FCSTD DOCUMENT  (FreeCAD 0.16R6712 (Git))
Label: Extruder_Assembly
License: CreativeCommons Attribution-ShareAlike
LicenseURL: http://creativecommons.org/licenses/by-sa/4.0/
objects: Part::FeaturePython×61, Part::Feature×27, Part::Compound×1
note: 89 computed .brp shape members not serialized (recipe doc carries the construction recipe); baked Part::Feature solids carry a one-line shape summary decoded from their .brp

FEATURE [Part::FeaturePython] tpge_extruderbase_01  # a2plus imported part (geometry in sourceFile) (typed FeaturePython)
  fixedPosition = true
  sourceFile = <userpath>/Downloads/The_Toranado_Precision_Geared_1.75mm_Extruder/files/tpge-extruderbase.FCStd
  timeLastImport = 1457562951
  updateColors = true
FEATURE [Part::FeaturePython] Knurl_Nut_01  # a2plus imported part (geometry in sourceFile) (typed FeaturePython)
  Placement = pos=(45.8,-17.25,27.12) rot=(0,1,0;1.5708rad)
  fixedPosition = false
  sourceFile = <userpath>/Downloads/The_Toranado_Precision_Geared_1.75mm_Extruder/files/Knurl Nut.FCStd
  timeLastImport = 1457566460
  updateColors = true
FEATURE [Part::FeaturePython] Knurl_Nut_002  # a2plus imported part (geometry in sourceFile) (typed FeaturePython)
  Placement = pos=(45.8,-17.25,4.12) rot=(0,1,0;1.5708rad)
  fixedPosition = false
  sourceFile = <userpath>/Downloads/The_Toranado_Precision_Geared_1.75mm_Extruder/files/Knurl Nut.FCStd
  timeLastImport = 1457566460
  updateColors = true
FEATURE [Part::FeaturePython] Knurl_Nut_003  # a2plus imported part (geometry in sourceFile) (typed FeaturePython)
  Placement = pos=(45.8,5.75,4.12) rot=(0,1,0;1.5708rad)
  fixedPosition = false
  sourceFile = <userpath>/Downloads/The_Toranado_Precision_Geared_1.75mm_Extruder/files/Knurl Nut.FCStd
  timeLastImport = 1457566460
  updateColors = true
FEATURE [Part::FeaturePython] Knurl_Nut_004  # a2plus imported part (geometry in sourceFile) (typed FeaturePython)
  Placement = pos=(-6.1,-20,6.7) rot=(0,1,0;1.5708rad)
  fixedPosition = false
  sourceFile = <userpath>/Downloads/The_Toranado_Precision_Geared_1.75mm_Extruder/files/Knurl Nut.FCStd
  timeLastImport = 1457566460
  updateColors = true
FEATURE [Part::FeaturePython] Knurl_Nut_005  # a2plus imported part (geometry in sourceFile) (typed FeaturePython)
  Placement = pos=(-2.8,-20,26) rot=(0,1,0;1.5708rad)
  fixedPosition = false
  sourceFile = <userpath>/Downloads/The_Toranado_Precision_Geared_1.75mm_Extruder/files/Knurl Nut.FCStd
  timeLastImport = 1457566460
  updateColors = true
FEATURE [Part::FeaturePython] PTFE_tubing_01  # a2plus imported part (geometry in sourceFile) (typed FeaturePython)
  Placement = pos=(-6.45,32.25,16.35) rot=(1,0,0;1.5708rad)
  fixedPosition = false
  sourceFile = <userpath>/Downloads/The_Toranado_Precision_Geared_1.75mm_Extruder/files/PTFE_tubing.FCStd
  timeLastImport = 1457567252
  updateColors = true
FEATURE [Part::FeaturePython] tpge_idler_tensioner_01  # a2plus imported part (geometry in sourceFile) (typed FeaturePython)
  Placement = pos=(-24,13,16.3) rot=(-1,0,0;1.5708rad)
  fixedPosition = false
  sourceFile = <userpath>/Downloads/The_Toranado_Precision_Geared_1.75mm_Extruder/files/tpge-idler-tensioner.FCStd
  timeLastImport = 1457567611
  updateColors = true
FEATURE [Part::FeaturePython] Screw  label="M3x30-Screw"  # Fasteners workbench fastener (typed FeaturePython)
  Placement = pos=(-20,18.5,7.8) rot=(0,-1,0;1.5708rad)
  diameter = 1
  invert = false
  length = 8
  matchOuter = false
  offset = 0
  thread = true
  type = 20
FEATURE [Part::FeaturePython] Nut001  label="M3-Nut"  # Fasteners workbench fastener (typed FeaturePython)
  Placement = pos=(0,18.5,7.8) rot=(0,1,0;1.5708rad)
  diameter = 4
  invert = false
  matchOuter = false
  offset = 0
  thread = true
  type = 1
FEATURE [Part::FeaturePython] Nut002  label="M3-Nut001"  # Fasteners workbench fastener (typed FeaturePython)
  Placement = pos=(0,18.5,24.7) rot=(0,1,0;1.5708rad)
  diameter = 4
  invert = false
  matchOuter = false
  offset = 0
  thread = true
  type = 1
FEATURE [Part::FeaturePython] Screw001  label="M3x30-Screw006"  # Fasteners workbench fastener (typed FeaturePython)
  Placement = pos=(-20,18.5,24.7) rot=(0,-1,0;1.5708rad)
  diameter = 1
  invert = false
  length = 8
  matchOuter = false
  offset = 0
  thread = true
  type = 20
FEATURE [Part::FeaturePython] tpge_gearprotector_01  # a2plus imported part (geometry in sourceFile) (typed FeaturePython)
  Placement = pos=(0,0,-0.000537556) rot=(0.999996,0.002921,0;3.14163rad)
  fixedPosition = false
  sourceFile = <userpath>/Downloads/The_Toranado_Precision_Geared_1.75mm_Extruder/files/tpge-gearprotector.FCStd
  timeLastImport = 1457613866
  updateColors = true
FEATURE [Part::FeaturePython] tpge_smallgearcover_01  # a2plus imported part (geometry in sourceFile) (typed FeaturePython)
  Placement = pos=(29.2,6.8663,-11.2036) rot=(0.999994,0.003491,0;3.14159rad)
  fixedPosition = false
  sourceFile = <userpath>/Downloads/The_Toranado_Precision_Geared_1.75mm_Extruder/files/tpge-smallgearcover.FCStd
  timeLastImport = 1457633503
  updateColors = true
FEATURE [Part::Feature] Fusion001_solid  label="Motor-with-connector-final"
  Placement = pos=(29.1,6.8,38.6) rot=(1,0,0;3.14159rad)
  shape: bbox 39.5 x 35.2 x 48 mm, 114 faces (baked)
FEATURE [Part::FeaturePython] Screw002  label="M3x14-Screw"  # Fasteners workbench fastener (typed FeaturePython)
  Placement = pos=(16.1,-6.2,-1.45) rot=(1,0,0;3.14159rad)
  diameter = 1
  invert = false
  length = 4
  matchOuter = false
  offset = 0
  thread = true
  type = 20
FEATURE [Part::FeaturePython] Screw003  label="M3x14-Screw013"  # Fasteners workbench fastener (typed FeaturePython)
  Placement = pos=(42.1,-6.2,-1.45) rot=(1,0,0;3.14159rad)
  diameter = 1
  invert = false
  length = 4
  matchOuter = false
  offset = 0
  thread = true
  type = 20
FEATURE [Part::FeaturePython] Screw004  label="M3x14-Screw014"  # Fasteners workbench fastener (typed FeaturePython)
  Placement = pos=(42.1,19.8,-1.45) rot=(1,0,0;3.14159rad)
  diameter = 1
  invert = false
  length = 4
  matchOuter = false
  offset = 0
  thread = true
  type = 20
FEATURE [Part::FeaturePython] Washer  label="M3-Washer"  # Fasteners workbench fastener (typed FeaturePython)
  Placement = pos=(42.1,19.8,10.05) rot=(0,0,1;0rad)
  diameter = 4
  invert = false
  matchOuter = false
  offset = 0
  type = 2
FEATURE [Part::FeaturePython] Washer001  label="M3-PTFE-Washer009"  # Fasteners workbench fastener (typed FeaturePython)
  Placement = pos=(16.1,-6.2,8.25) rot=(0,0,1;0rad)
  diameter = 1
  invert = false
  matchOuter = false
  offset = 0
  type = 3
FEATURE [Part::FeaturePython] Washer002  label="M3-PTFE-Washer010"  # Fasteners workbench fastener (typed FeaturePython)
  Placement = pos=(42.1,19.8,8.25) rot=(0,0,1;0rad)
  diameter = 1
  invert = false
  matchOuter = false
  offset = 0
  type = 3
FEATURE [Part::FeaturePython] Washer003  label="M3-PTFE-Washer011"  # Fasteners workbench fastener (typed FeaturePython)
  Placement = pos=(42.1,-6.2,8.25) rot=(0,0,1;0rad)
  diameter = 1
  invert = false
  matchOuter = false
  offset = 0
  type = 3
FEATURE [Part::FeaturePython] Washer004  label="M3-PTFE-Washer012"  # Fasteners workbench fastener (typed FeaturePython)
  Placement = pos=(16.1,-6.2,9.15) rot=(0,0,1;0rad)
  diameter = 1
  invert = false
  matchOuter = false
  offset = 0
  type = 3
FEATURE [Part::FeaturePython] Washer005  label="M3-PTFE-Washer013"  # Fasteners workbench fastener (typed FeaturePython)
  Placement = pos=(42.1,19.8,9.15) rot=(0,0,1;0rad)
  diameter = 1
  invert = false
  matchOuter = false
  offset = 0
  type = 3
FEATURE [Part::FeaturePython] Washer006  label="M3-PTFE-Washer014"  # Fasteners workbench fastener (typed FeaturePython)
  Placement = pos=(42.1,-6.2,9.15) rot=(0,0,1;0rad)
  diameter = 1
  invert = false
  matchOuter = false
  offset = 0
  type = 3
FEATURE [Part::FeaturePython] Washer007  label="M3-PTFE-Washer006"  # Fasteners workbench fastener (typed FeaturePython)
  Placement = pos=(16.1,-6.2,-0.9) rot=(0,0,1;0rad)
  diameter = 1
  invert = false
  matchOuter = false
  offset = 0
  type = 3
FEATURE [Part::FeaturePython] Washer008  label="M3-PTFE-Washer007"  # Fasteners workbench fastener (typed FeaturePython)
  Placement = pos=(42.1,19.8,-0.9) rot=(0,0,1;0rad)
  diameter = 1
  invert = false
  matchOuter = false
  offset = 0
  type = 3
FEATURE [Part::FeaturePython] Washer009  label="M3-PTFE-Washer008"  # Fasteners workbench fastener (typed FeaturePython)
  Placement = pos=(42.1,-6.2,-0.9) rot=(0,0,1;0rad)
  diameter = 1
  invert = false
  matchOuter = false
  offset = 0
  type = 3
FEATURE [Part::FeaturePython] Washer010  label="M3-Washer021"  # Fasteners workbench fastener (typed FeaturePython)
  Placement = pos=(42.1,-6.2,10.05) rot=(0,0,1;0rad)
  diameter = 4
  invert = false
  matchOuter = false
  offset = 0
  type = 2
FEATURE [Part::FeaturePython] Washer011  label="M3-Washer022"  # Fasteners workbench fastener (typed FeaturePython)
  Placement = pos=(16.1,-6.2,10.05) rot=(0,0,1;0rad)
  diameter = 4
  invert = false
  matchOuter = false
  offset = 0
  type = 2
FEATURE [Part::Feature] Cut_solid  label="Cut (Solid)"
  Placement = pos=(42.1,-6.2,0) rot=(0,0,1;0rad)
  shape: bbox 5 x 5 x 8.25 mm, 4 faces (baked)
FEATURE [Part::Feature] Cut_solid001  label="Cut (Solid)001"
  Placement = pos=(42.1,19.8,0) rot=(0,0,1;0rad)
  shape: bbox 5 x 5 x 8.25 mm, 4 faces (baked)
FEATURE [Part::Feature] Cut_solid002  label="Cut (Solid)002"
  Placement = pos=(16.1,-6.2,0) rot=(0,0,1;0rad)
  shape: bbox 5 x 5 x 8.25 mm, 4 faces (baked)
FEATURE [Part::FeaturePython] Washer012  label="M3-Washer026"  # Fasteners workbench fastener (typed FeaturePython)
  Placement = pos=(42.1,-6.2,-1.45) rot=(0,0,1;0rad)
  diameter = 4
  invert = false
  matchOuter = false
  offset = 0
  type = 2
FEATURE [Part::FeaturePython] Washer013  label="M3-Washer027"  # Fasteners workbench fastener (typed FeaturePython)
  Placement = pos=(16.1,-6.2,-1.45) rot=(0,0,1;0rad)
  diameter = 4
  invert = false
  matchOuter = false
  offset = 0
  type = 2
FEATURE [Part::FeaturePython] Washer014  label="M3-Washer028"  # Fasteners workbench fastener (typed FeaturePython)
  Placement = pos=(42.1,19.8,-1.45) rot=(0,0,1;0rad)
  diameter = 4
  invert = false
  matchOuter = false
  offset = 0
  type = 2
FEATURE [Part::FeaturePython] tpge_40mmfanduct_bltouch_01  # a2plus imported part (geometry in sourceFile) (typed FeaturePython)
  Placement = pos=(-0.8,-70,16.35) rot=(-1,0,0;1.5708rad)
  fixedPosition = false
  sourceFile = <userpath>/Downloads/The_Toranado_Precision_Geared_1.75mm_Extruder/files/tpge-40mmfanduct-bltouch.FCStd
  timeLastImport = 1457565339
  updateColors = true
FEATURE [Part::FeaturePython] Washer015  label="M3-Washer029"  # Fasteners workbench fastener (typed FeaturePython)
  Placement = pos=(11.78,-25.3,6.73) rot=(0,1,0;1.5708rad)
  diameter = 4
  invert = false
  matchOuter = false
  offset = 0
  type = 2
FEATURE [Part::FeaturePython] Washer016  label="M3-Washer030"  # Fasteners workbench fastener (typed FeaturePython)
  Placement = pos=(11.78,-25.3,26) rot=(0,1,0;1.5708rad)
  diameter = 4
  invert = false
  matchOuter = false
  offset = 0
  type = 2
FEATURE [Part::Feature] Cut_solid003  label="M3x18 Self-Tapping"
  Placement = pos=(-47.0102,32.1919,-31.9418) rot=(0,0,1;0rad)
  shape: bbox 5.6 x 5.6 x 20.3 mm, 130 faces (baked)
FEATURE [Part::Feature] Cut_solid004  label="M3x14 Self-Tapping"
  Placement = pos=(30.5682,-10.6081,-53.9102) rot=(0,-1,0;1.5708rad)
  shape: bbox 16.84 x 5.6 x 5.6 mm, 108 faces (baked)
FEATURE [Part::Feature] Cut_solid005  label="M3x5 Self-Tapping"
  Placement = pos=(-91.4,-2.5,-20) rot=(0,0,1;0rad)
  shape: bbox 5.6 x 5.6 x 7.878 mm, 61 faces (baked)
FEATURE [Part::Feature] Cut_solid006  label="M3x18 Self-Tapping001"
  Placement = pos=(-48.9102,3.6919,-31.9418) rot=(0,0,1;0rad)
  shape: bbox 5.6 x 5.6 x 20.3 mm, 130 faces (baked)
FEATURE [Part::Feature] Cut_solid007  label="M3x14 Self-Tapping001"
  Placement = pos=(30.5682,-10.6081,-73.1802) rot=(0,-1,0;1.5708rad)
  shape: bbox 16.84 x 5.6 x 5.6 mm, 108 faces (baked)
FEATURE [Part::Feature] Cut_solid008  label="M3x5 Self-Tapping001"
  Placement = pos=(-88.2,34.5,-20) rot=(0,0,1;0rad)
  shape: bbox 5.6 x 5.6 x 7.878 mm, 61 faces (baked)
FEATURE [Part::FeaturePython] Robson_Gear_01001  label="Robinson Racing #2019 19T 48p Steel Pinion Gear"  # a2plus imported part (geometry in sourceFile) (typed FeaturePython)
  Placement = pos=(24.8934,-54.2021,14.7336) rot=(0,0,1;0rad)
  fixedPosition = false
  sourceFile = <userpath>/Downloads/The_Toranado_Precision_Geared_1.75mm_Extruder/files/Robson-Gear.FCStd
  timeLastImport = 1457651616
  updateColors = true
FEATURE [Part::FeaturePython] Acetal_Main_Gear_01  # a2plus imported part (geometry in sourceFile) (typed FeaturePython)
  Placement = pos=(0,0,-8.8) rot=(0,0,1;0.008727rad)
  fixedPosition = false
  sourceFile = <userpath>/Downloads/The_Toranado_Precision_Geared_1.75mm_Extruder/files/Acetal Main Gear.FCStd
  timeLastImport = 1457654570
  updateColors = true
FEATURE [Part::FeaturePython] Adapter_01  # a2plus imported part (geometry in sourceFile) (typed FeaturePython)
  Placement = pos=(0,0,-15.785) rot=(0,0,1;0rad)
  fixedPosition = false
  sourceFile = <userpath>/Downloads/The_Toranado_Precision_Geared_1.75mm_Extruder/files/Adapter.FCStd
  timeLastImport = 1457654163
  updateColors = true
FEATURE [Part::FeaturePython] tpge_spacer_wprintpad_01  # a2plus imported part (geometry in sourceFile) (typed FeaturePython)
  Placement = pos=(0,0,-6.26) rot=(0,0,1;0rad)
  fixedPosition = false
  sourceFile = <userpath>/Downloads/The_Toranado_Precision_Geared_1.75mm_Extruder/files/tpge-spacer-wprintpad.FCStd
  timeLastImport = 1457655122
  updateColors = true
FEATURE [Part::Feature] Chamfer_solid  label="Chamfer (Solid)"
  Placement = pos=(0,0,-16) rot=(0,0,1;0rad)
  shape: bbox 5 x 5 x 50 mm, 5 faces (baked)
FEATURE [Part::FeaturePython] MK7_igs1_01  # a2plus imported part (geometry in sourceFile) (typed FeaturePython)
  Placement = pos=(0,0,8.8) rot=(0,0.707107,0.707107;3.14159rad)
  fixedPosition = true
  sourceFile = <userpath>/Downloads/The_Toranado_Precision_Geared_1.75mm_Extruder/files/MK7.igs
  timeLastImport = 1392244751
  updateColors = true
FEATURE [Part::FeaturePython] din_en_iso_4026_m3x3_45h_stp1_01  # a2plus imported part (geometry in sourceFile) (typed FeaturePython)
  Placement = pos=(-7,0,11.8) rot=(0,-1,0;1.5708rad)
  fixedPosition = false
  sourceFile = <userpath>/Downloads/The_Toranado_Precision_Geared_1.75mm_Extruder/files/din_en_iso_4026-m3x3-45h.stp
  timeLastImport = 1457661076
  updateColors = true
FEATURE [Part::FeaturePython] DIN625_1_625_ZZ_01  # a2plus imported part (geometry in sourceFile) (typed FeaturePython)
  fixedPosition = false
  sourceFile = /Applications/FreeCAD.app/Contents/Mod/FreeCAD-library/Mechanical Parts/Bearings/DIN625-1_625-ZZ.fcstd
  timeLastImport = 1458081288
  updateColors = true
FEATURE [Part::FeaturePython] DIN625_1_625_ZZ_002  # a2plus imported part (geometry in sourceFile) (typed FeaturePython)
  Placement = pos=(0,0,24) rot=(0,0,1;0rad)
  fixedPosition = false
  sourceFile = /Applications/FreeCAD.app/Contents/Mod/FreeCAD-library/Mechanical Parts/Bearings/DIN625-1_625-ZZ.fcstd
  timeLastImport = 1458081288
  updateColors = true
FEATURE [Part::FeaturePython] tpge_bearingcover_01  # a2plus imported part (geometry in sourceFile) (typed FeaturePython)
  Placement = pos=(0,0,23.45) rot=(0,0,1;0rad)
  fixedPosition = false
  sourceFile = <userpath>/Downloads/The_Toranado_Precision_Geared_1.75mm_Extruder/files/tpge-bearingcover.FCStd
  timeLastImport = 1458081563
  updateColors = true
FEATURE [Part::FeaturePython] tpge_shaftcollar_01  # a2plus imported part (geometry in sourceFile) (typed FeaturePython)
  Placement = pos=(0,0,29) rot=(0,0,1;3.14159rad)
  fixedPosition = false
  sourceFile = <userpath>/Downloads/The_Toranado_Precision_Geared_1.75mm_Extruder/files/tpge-shaftcollar.FCStd
  timeLastImport = 1458082026
  updateColors = true
FEATURE [Part::FeaturePython] din_en_iso_4026_m3x3_45h_stp1_002  # a2plus imported part (geometry in sourceFile) (typed FeaturePython)
  Placement = pos=(-7,0,31.8) rot=(0,-1,0;1.5708rad)
  fixedPosition = false
  sourceFile = <userpath>/Downloads/The_Toranado_Precision_Geared_1.75mm_Extruder/files/din_en_iso_4026-m3x3-45h.stp
  timeLastImport = 1457661076
  updateColors = true
FEATURE [Part::FeaturePython] tpge_decorationcover_01  # a2plus imported part (geometry in sourceFile) (typed FeaturePython)
  Placement = pos=(0,0,30) rot=(0,0,1;0rad)
  fixedPosition = false
  sourceFile = <userpath>/Downloads/The_Toranado_Precision_Geared_1.75mm_Extruder/files/tpge-decorationcover.FCStd
  timeLastImport = 1457658208
  updateColors = true
FEATURE [Part::Feature] Cut_solid009  label="M3x14 Self-Tapping002"
  Placement = pos=(71.6,26.5,54.5382) rot=(0,1,0;3.14159rad)
  shape: bbox 5.6 x 5.6 x 16.84 mm, 108 faces (baked)
FEATURE [Part::Feature] Cut_solid010  label="M3x18 Self-Tapping002"
  Placement = pos=(86.7,4.65,54.7382) rot=(0,1,0;3.14159rad)
  shape: bbox 5.6 x 5.6 x 20.3 mm, 130 faces (baked)
FEATURE [Part::Feature] Cut_solid011  label="M3x18 Self-Tapping003"
  Placement = pos=(86.7,24.45,54.7382) rot=(0,1,0;3.14159rad)
  shape: bbox 5.6 x 5.6 x 20.3 mm, 130 faces (baked)
FEATURE [Part::FeaturePython] tpge_idler_wprintpad_01  # a2plus imported part (geometry in sourceFile) (typed FeaturePython)
  Placement = pos=(-12.7,-0.5,16.4) rot=(0,-1,0;1.5708rad)
  fixedPosition = false
  sourceFile = <userpath>/Downloads/The_Toranado_Precision_Geared_1.75mm_Extruder/files/tpge-idler-wprintpad.FCStd
  timeLastImport = 1457658649
  updateColors = true
FEATURE [Part::FeaturePython] E3D_v6_01  # a2plus imported part (geometry in sourceFile) (typed FeaturePython)
  Placement = pos=(-6,-56.35,16.3) rot=(0,0.707107,-0.707107;3.14159rad)
  fixedPosition = false
  sourceFile = <userpath>/Downloads/The_Toranado_Precision_Geared_1.75mm_Extruder/files/E3D-v6.FCStd
  timeLastImport = 1458083703
  updateColors = true
FEATURE [Part::FeaturePython] E3dv6_3omm_fan_duct_01  # a2plus imported part (geometry in sourceFile) (typed FeaturePython)
  Placement = pos=(-6,-60.5,16.3) rot=(0,0,1;0rad)
  fixedPosition = false
  sourceFile = <userpath>/Downloads/The_Toranado_Precision_Geared_1.75mm_Extruder/files/E3dv6 3omm fan duct.FCStd
  timeLastImport = 1458084071
  updateColors = true
FEATURE [Part::FeaturePython] _0x30x10_12vdc_cooling_fan_01  # a2plus imported part (geometry in sourceFile) (typed FeaturePython)
  Placement = pos=(-6,-45.5,31.3) rot=(0,0,1;0rad)
  fixedPosition = false
  sourceFile = <userpath>/Downloads/The_Toranado_Precision_Geared_1.75mm_Extruder/files/30x30x10 12vdc cooling fan.FCStd
  timeLastImport = 1458084260
  updateColors = true
FEATURE [Part::FeaturePython] tpge_fancover_30mm_01  # a2plus imported part (geometry in sourceFile) (typed FeaturePython)
  Placement = pos=(-31,-45.5,16.3) rot=(0,-1,0;1.5708rad)
  fixedPosition = false
  sourceFile = <userpath>/Downloads/The_Toranado_Precision_Geared_1.75mm_Extruder/files/tpge-fancover-30mm.FCStd
  timeLastImport = 1458084461
  updateColors = true
FEATURE [Part::Feature] Cut_solid012  label="M3x18 Self-Tapping004"
  Placement = pos=(-51.6382,-18.8081,84.2102) rot=(0,1,0;1.5708rad)
  shape: bbox 20.3 x 5.6 x 5.6 mm, 130 faces (baked)
FEATURE [Part::Feature] Cut_solid013  label="M3x18 Self-Tapping005"
  Placement = pos=(-51.6382,-18.8081,108.21) rot=(0,1,0;1.5708rad)
  shape: bbox 20.3 x 5.6 x 5.6 mm, 130 faces (baked)
FEATURE [Part::Feature] Cut_solid014  label="M3x18 Self-Tapping006"
  Placement = pos=(-51.6382,-42.8081,84.2102) rot=(0,1,0;1.5708rad)
  shape: bbox 20.3 x 5.6 x 5.6 mm, 130 faces (baked)
FEATURE [Part::Feature] Cut_solid015  label="M3x18 Self-Tapping007"
  Placement = pos=(-51.6382,-42.8081,108.21) rot=(0,1,0;1.5708rad)
  shape: bbox 20.3 x 5.6 x 5.6 mm, 130 faces (baked)
FEATURE [Part::FeaturePython] tpge_clamp_hotend_01  # a2plus imported part (geometry in sourceFile) (typed FeaturePython)
  Placement = pos=(-5.06,-29.4,16.35) rot=(-0.57735,0.57735,0.57735;2.0944rad)
  fixedPosition = false
  sourceFile = <userpath>/Downloads/The_Toranado_Precision_Geared_1.75mm_Extruder/files/tpge-clamp-hotend.FCStd
  timeLastImport = 1458085068
  updateColors = true
FEATURE [Part::FeaturePython] Screw007  label="M3x30-Screw004"  # Fasteners workbench fastener (typed FeaturePython)
  Placement = pos=(-21.96,-20,6.7) rot=(0,-1,0;1.5708rad)
  diameter = 1
  invert = false
  length = 8
  matchOuter = false
  offset = 0
  thread = true
  type = 20
FEATURE [Part::FeaturePython] Screw008  label="M3x30-Screw005"  # Fasteners workbench fastener (typed FeaturePython)
  Placement = pos=(-21.96,-20,26) rot=(0,-1,0;1.5708rad)
  diameter = 1
  invert = false
  length = 8
  matchOuter = false
  offset = 0
  thread = true
  type = 20
FEATURE [Part::Feature] Chamfer_solid001  label="Chamfer (Solid)001"
  shape: bbox 5 x 5 x 25 mm, 5 faces (baked)
FEATURE [Part::FeaturePython] DIN625_1_625_ZZ_003  # a2plus imported part (geometry in sourceFile) (typed FeaturePython)
  Placement = pos=(-14,0,14) rot=(0,0,1;0rad)
  fixedPosition = false
  sourceFile = /Applications/FreeCAD.app/Contents/Mod/FreeCAD-library/Mechanical Parts/Bearings/DIN625-1_625-ZZ.fcstd
  timeLastImport = 1458081288
  updateColors = true
FEATURE [Part::FeaturePython] Screw009  label="M3x20-Screw"  # Fasteners workbench fastener (typed FeaturePython)
  Placement = pos=(-24.2057,-10.176,26.9) rot=(0,0,1;0rad)
  diameter = 1
  invert = false
  length = 6
  matchOuter = false
  offset = 0
  thread = true
  type = 20
FEATURE [Part::FeaturePython] tpge_gearcover_94t_01  # a2plus imported part (geometry in sourceFile) (typed FeaturePython)
  Placement = pos=(0,0,-8.285) rot=(-0.233445,0.97237,0;3.14159rad)
  fixedPosition = false
  sourceFile = <userpath>/Downloads/The_Toranado_Precision_Geared_1.75mm_Extruder/files/tpge-gearcover-94t.FCStd
  timeLastImport = 1458086769
  updateColors = true
FEATURE [Part::FeaturePython] tpge_hubcover_wscrews_01  # a2plus imported part (geometry in sourceFile) (typed FeaturePython)
  Placement = pos=(0,0,-15.785) rot=(0.845728,0.533615,0;3.14159rad)
  fixedPosition = false
  sourceFile = <userpath>/Downloads/The_Toranado_Precision_Geared_1.75mm_Extruder/files/tpge-hubcover-wscrews.FCStd
  timeLastImport = 1458086978
  updateColors = true
FEATURE [Part::Feature] M3x10_Screw_Copy  label="6-32 3/8” Truss-Head Screw"
  Placement = pos=(9.77863,0.0853368,-5.625) rot=(0,0,1;0rad)
  shape: bbox 7.5 x 7.5 x 12.29 mm, 28 faces (baked)
FEATURE [Part::Feature] M3x10_Screw001_Copy  label="6-32 3/8” Truss-Head Screw001"
  Placement = pos=(-9.77863,-0.0853368,-5.625) rot=(0,0,1;0rad)
  shape: bbox 7.5 x 7.5 x 12.29 mm, 28 faces (baked)
FEATURE [Part::Feature] M3x10_Screw_Copy001  label="6-32 3/8” Truss-Head Screw002"
  Placement = pos=(9.779,0,-18.185) rot=(0,1,0;3.14159rad)
  shape: bbox 7.5 x 7.5 x 12.29 mm, 28 faces (baked)
FEATURE [Part::Feature] M3x10_Screw_Copy002  label="6-32 3/8” Truss-Head Screw003"
  Placement = pos=(-9.779,0,-18.185) rot=(0,1,0;3.14159rad)
  shape: bbox 7.5 x 7.5 x 12.29 mm, 28 faces (baked)
FEATURE [Part::FeaturePython] _0x40x10_12vdc_cooling_fan_01  # a2plus imported part (geometry in sourceFile) (typed FeaturePython)
  Placement = pos=(30.3058,-46.8532,16.1874) rot=(0.171085,-0.970273,0.171171;1.60044rad)
  fixedPosition = false
  sourceFile = <userpath>/Downloads/The_Toranado_Precision_Geared_1.75mm_Extruder/files/40x40x10 12vdc cooling fan.FCStd
  timeLastImport = 1458087591
  updateColors = true
FEATURE [Part::FeaturePython] tpge_fancover_40mm_01  # a2plus imported part (geometry in sourceFile) (typed FeaturePython)
  Placement = pos=(30.3008,-46.8267,16.1873) rot=(-0.171095,0.97033,0.17084;1.60138rad)
  fixedPosition = false
  sourceFile = <userpath>/Downloads/The_Toranado_Precision_Geared_1.75mm_Extruder/files/tpge-fancover-40mm.FCStd
  timeLastImport = 1458088049
  updateColors = true
FEATURE [Part::Feature] Cut_solid016  label="M3x18 Self-Tapping008"
  Placement = pos=(30.2889,13.9373,-37.8949) rot=(0.341855,-0.939753,0;1.5703rad)
  shape: bbox 19.69 x 10.58 x 6.732 mm, 130 faces (baked)
FEATURE [Part::Feature] Cut_solid017  label="M3x18 Self-Tapping009"
  Placement = pos=(41.2243,-16.1241,-37.8952) rot=(0.341855,-0.939753,0;1.5703rad)
  shape: bbox 19.69 x 10.58 x 6.732 mm, 130 faces (baked)
FEATURE [Part::Feature] Cut_solid018  label="M3x18 Self-Tapping010"
  Placement = pos=(30.2739,13.932,-69.8844) rot=(0.341855,-0.939753,0;1.5703rad)
  shape: bbox 19.69 x 10.58 x 6.732 mm, 130 faces (baked)
FEATURE [Part::Feature] Cut_solid019  label="M3x18 Self-Tapping011"
  Placement = pos=(41.2096,-16.1302,-69.8846) rot=(0.341855,-0.939753,0;1.5703rad)
  shape: bbox 19.69 x 10.58 x 6.732 mm, 130 faces (baked)
FEATURE [Part::Compound] Compound
  Links = -> [Cut_solid019,Cut_solid017,tpge_fancover_40mm_01,Washer003,Washer002,Washer001,Washer,Screw004,Screw003,Screw002,Fusion001_solid,tpge_smallgearcover_01,M3x10_Screw_Copy002,M3x10_Screw_Copy001,_0x40x10_12vdc_cooling_fan_01,Screw,Knurl_Nut_005,tpge_idler_tensioner_01,Screw001,tpge_gearprotector_01,PTFE_tubing_01,Knurl_Nut_003,tpge_extruderbase_01,Knurl_Nut_002,Knurl_Nut_004,Cut_solid018,Cut_solid016,+61 more]
